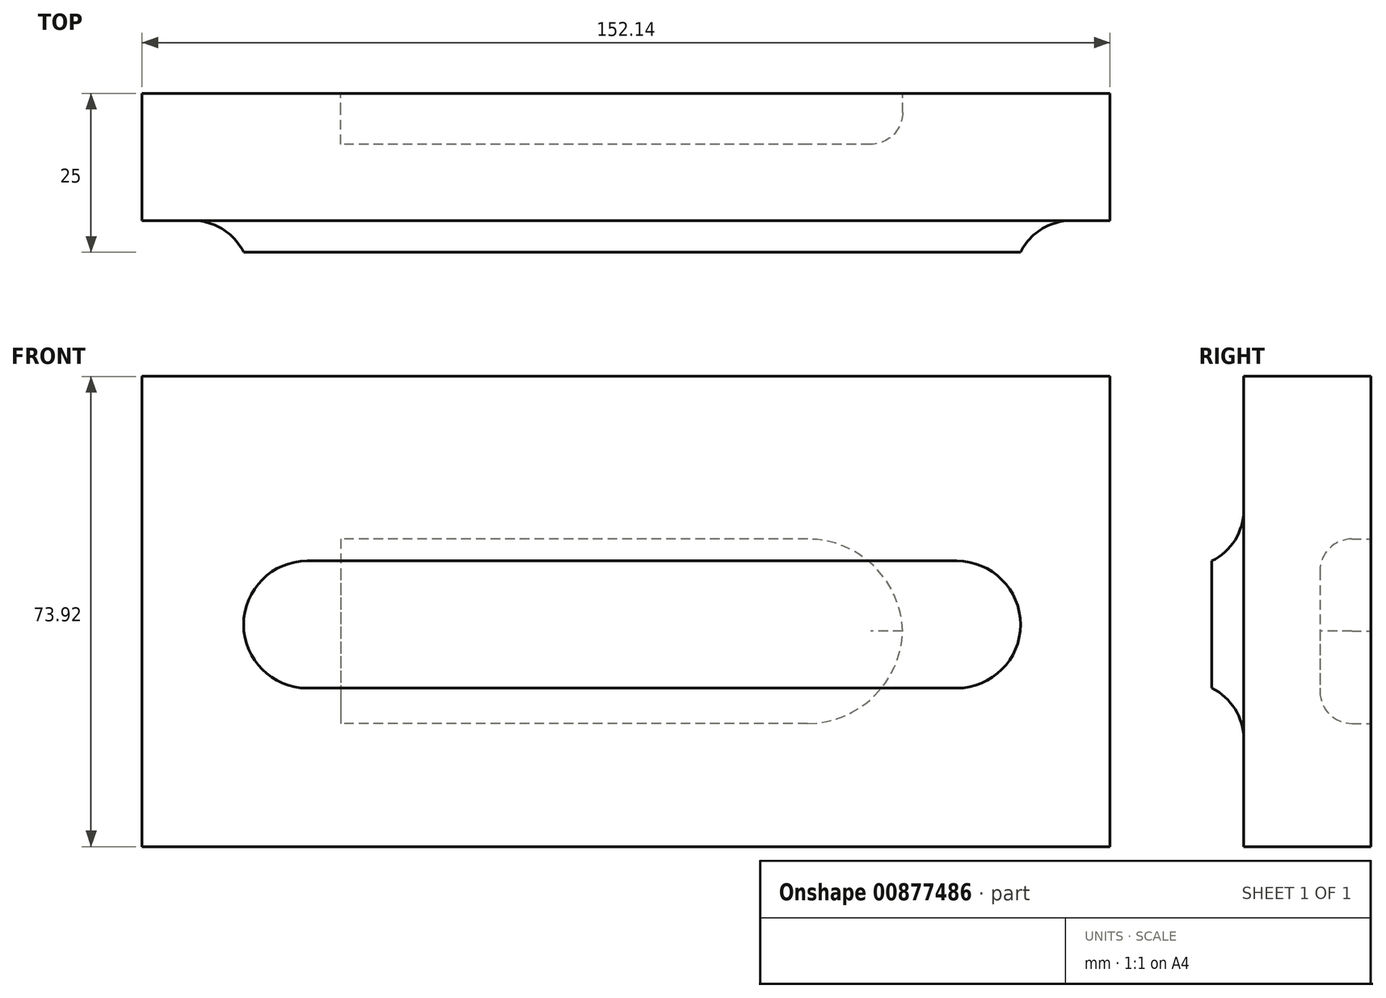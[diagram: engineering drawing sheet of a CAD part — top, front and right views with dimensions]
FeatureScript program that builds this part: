
annotation { "Feature Type Name" : "Feature", "Feature Type Description" : "" }
export const myFeature = defineFeature(function(context is Context, id is Id, definition is map)
    precondition{}
    {
        {
            var Q0;
            Q0=qCreatedBy(makeId("Front.planeOp"),FACE);
            var sketch = newSketch(context, id + "F0", { "sketchPlane" : qUnion([Q0])});
            skLineSegment(sketch, "E0.bottom", {"start": v(-95.94, 26.18) * mm, "end": v(56.2, 26.18) * mm});
            skLineSegment(sketch, "E0.top", {"start": v(-95.94, -47.74) * mm, "end": v(56.2, -47.74) * mm});
            skLineSegment(sketch, "E0.left", {"start": v(-95.94, 26.18) * mm, "end": v(-95.94, -47.74) * mm});
            skLineSegment(sketch, "E0.right", {"start": v(56.2, 26.18) * mm, "end": v(56.2, -47.74) * mm});
            skSolve(sketch);
        }
        {
            var Q0;
            Q0=makeQuery(id+"F0.imprint","IMPRINT",FACE,{"disambiguationData":[TD([[makeQuery(id+"F0.imprint","IMPRINT",EDGE,{"derivedFrom":sQuery(id+"F0.wireOp",EDGE,"E0.bottom")}),-1.0]])]});
            extrude(context, id + "F1", {"entities" : qUnion([Q0]), "depth" : 25 * mm, "offsetDistance" : 25 * mm});
        }
        {
            var Q0;
            Q0=makeQuery(id+"F1.opExtrude","CAP_FACE",FACE,{"disambiguationData":[OSD([sQuery(id+"F0.wireOp",EDGE,"E0.bottom"),sQuery(id+"F0.wireOp",EDGE,"E0.top"),sQuery(id+"F0.wireOp",EDGE,"E0.left"),sQuery(id+"F0.wireOp",EDGE,"E0.right")])],"isStart":false});
            var sketch = newSketch(context, id + "F2", { "sketchPlane" : qUnion([Q0])});
            skLineSegment(sketch, "E1", {"start": v(-69.99, -12.84) * mm, "end": v(32.12, -12.84) * mm});
            skArc(sketch, "E2.0.startCap", {"start": v(-69.99, -22.84) * mm, "mid": v(-79.99, -12.84) * mm, "end": v(-69.99, -2.84) * mm});
            skArc(sketch, "E2.0.endCap", {"start": v(32.12, -2.84) * mm, "mid": v(42.12, -12.84) * mm, "end": v(32.12, -22.84) * mm});
            skLineSegment(sketch, "E2.0.left", {"start": v(-69.99, -2.84) * mm, "end": v(32.12, -2.84) * mm});
            skLineSegment(sketch, "E2.0.right", {"start": v(-69.99, -22.84) * mm, "end": v(32.12, -22.84) * mm});
            skSolve(sketch);
        }
        {
            var Q0;
            Q0=makeQuery(id+"F2.imprint","IMPRINT",FACE,{"disambiguationData":[TD([[makeQuery(id+"F2.imprint","IMPRINT",EDGE,{"derivedFrom":sQuery(id+"F2.wireOp",EDGE,"E2.0.startCap")}),-1.0]])]});
            extrude(context, id + "F3", {"entities" : qUnion([Q0]), "operationType" : NewBodyOperationType.REMOVE, "oppositeDirection" : true, "depth" : 5 * mm, "offsetDistance" : 25 * mm});
        }
        {
            var Q0;
            Q0=makeQuery(id+"F3.boolean.opBoolean","COPY",EDGE,{"derivedFrom":makeQuery(id+"F3.opExtrude","CAP_EDGE",EDGE,{"disambiguationData":[OSD([sQuery(id+"F2.wireOp",EDGE,"E2.0.right")])],"isStart":false})});
            fillet(context, id + "F4", {"entities" : qUnion([Q0]), "radius" : 8.93 * mm, "tangentPropagation" : true, "allowEdgeOverflow" : false});
        }
        {
            var Q0;
            Q0=makeQuery(id+"F1.opExtrude","CAP_FACE",FACE,{"disambiguationData":[OSD([sQuery(id+"F0.wireOp",EDGE,"E0.bottom"),sQuery(id+"F0.wireOp",EDGE,"E0.top"),sQuery(id+"F0.wireOp",EDGE,"E0.left"),sQuery(id+"F0.wireOp",EDGE,"E0.right")])],"isStart":true});
            var sketch = newSketch(context, id + "F5", { "sketchPlane" : qUnion([Q0])});
            skLineSegment(sketch, "E3.bottom", {"start": v(-23.6, 0.62) * mm, "end": v(64.71, 0.62) * mm});
            skLineSegment(sketch, "E3.top", {"start": v(-23.6, -28.38) * mm, "end": v(64.71, -28.38) * mm});
            skLineSegment(sketch, "E3.left", {"start": v(-23.6, 0.62) * mm, "end": v(-23.6, -28.38) * mm});
            skLineSegment(sketch, "E3.right", {"start": v(64.71, 0.62) * mm, "end": v(64.71, -28.38) * mm});
            skSolve(sketch);
        }
        {
            var Q0;
            Q0=makeQuery(id+"F5.imprint","IMPRINT",FACE,{"disambiguationData":[TD([[makeQuery(id+"F5.imprint","IMPRINT",EDGE,{"derivedFrom":sQuery(id+"F5.wireOp",EDGE,"E3.bottom")}),-1.0]])]});
            extrude(context, id + "F6", {"entities" : qUnion([Q0]), "operationType" : NewBodyOperationType.REMOVE, "oppositeDirection" : true, "depth" : 8 * mm, "offsetDistance" : 25 * mm});
        }
        {
            var Q0;
            Q0=makeQuery(id+"F6.boolean.opBoolean","COPY",EDGE,{"derivedFrom":makeQuery(id+"F6.opExtrude","SWEPT_EDGE",EDGE,{"disambiguationData":[OSD([sQuery(id+"F5.wireOp",EDGE,"E3.top"),sQuery(id+"F5.wireOp",EDGE,"E3.left")])]})});
            var Q1;
            Q1=makeQuery(id+"F6.boolean.opBoolean","COPY",EDGE,{"derivedFrom":makeQuery(id+"F6.opExtrude","SWEPT_EDGE",EDGE,{"disambiguationData":[OSD([sQuery(id+"F5.wireOp",EDGE,"E3.bottom"),sQuery(id+"F5.wireOp",EDGE,"E3.left")])]})});
            fillet(context, id + "F7", {"entities" : qUnion([Q0, Q1]), "radius" : 14.97 * mm, "tangentPropagation" : true, "allowEdgeOverflow" : false});
        }
        {
            var Q0;
            {var subQ0=sQuery(id+"F5.wireOp",EDGE,"E3.left");var subQ1=sQuery(id+"F5.wireOp",EDGE,"E3.bottom");Q0=makeQuery(id+"F7.opFillet","BLEND_EDGE",EDGE,{"blendedFrom":[makeQuery(id+"F6.boolean.opBoolean","COPY",EDGE,{"derivedFrom":makeQuery(id+"F6.opExtrude","SWEPT_EDGE",EDGE,{"disambiguationData":[OSD([subQ1,subQ0])]})}),makeQuery(id+"F6.boolean.opBoolean","COPY",FACE,{"derivedFrom":makeQuery(id+"F6.opExtrude","CAP_FACE",FACE,{"disambiguationData":[OSD([subQ1,sQuery(id+"F5.wireOp",EDGE,"E3.top"),subQ0,sQuery(id+"F5.wireOp",EDGE,"E3.right")])],"isStart":false})})],"blendedInto":[makeQuery(id+"F6.boolean.opBoolean","COPY",FACE,{"derivedFrom":makeQuery(id+"F6.opExtrude","CAP_FACE",FACE,{"disambiguationData":[OSD([subQ1,sQuery(id+"F5.wireOp",EDGE,"E3.top"),subQ0,sQuery(id+"F5.wireOp",EDGE,"E3.right")])],"isStart":false})})]});}
            var Q1;
            {var subQ0=sQuery(id+"F5.wireOp",EDGE,"E3.left");var subQ1=sQuery(id+"F5.wireOp",EDGE,"E3.top");Q1=makeQuery(id+"F7.opFillet","BLEND_EDGE",EDGE,{"blendedFrom":[makeQuery(id+"F6.boolean.opBoolean","COPY",EDGE,{"derivedFrom":makeQuery(id+"F6.opExtrude","SWEPT_EDGE",EDGE,{"disambiguationData":[OSD([subQ1,subQ0])]})}),makeQuery(id+"F6.boolean.opBoolean","COPY",FACE,{"derivedFrom":makeQuery(id+"F6.opExtrude","CAP_FACE",FACE,{"disambiguationData":[OSD([sQuery(id+"F5.wireOp",EDGE,"E3.bottom"),subQ1,subQ0,sQuery(id+"F5.wireOp",EDGE,"E3.right")])],"isStart":false})})],"blendedInto":[makeQuery(id+"F6.boolean.opBoolean","COPY",FACE,{"derivedFrom":makeQuery(id+"F6.opExtrude","CAP_FACE",FACE,{"disambiguationData":[OSD([sQuery(id+"F5.wireOp",EDGE,"E3.bottom"),subQ1,subQ0,sQuery(id+"F5.wireOp",EDGE,"E3.right")])],"isStart":false})})]});}
            fillet(context, id + "F8", {"entities" : qUnion([Q0, Q1]), "radius" : 5 * mm, "tangentPropagation" : true, "allowEdgeOverflow" : false});
        }
    });
